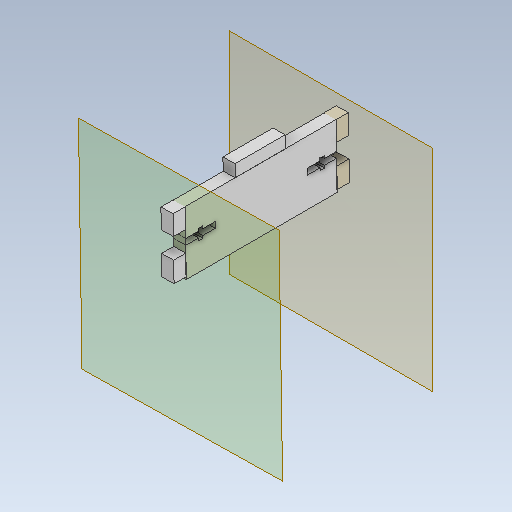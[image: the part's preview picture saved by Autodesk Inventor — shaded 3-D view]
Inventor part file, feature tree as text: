
AUTODESK INVENTOR PART (.ipt)
format: ipt  version: 2021.1 (Build 251245010, 245A)  size: 203,776 bytes
history: native  units: mm
features: reference x18, other x8, extrude x5, sketch x5, projected_geometry x1
ambient origin geometry x8: Origin, YZ Plane, XZ Plane, XY Plane, X Axis, Y Axis, Z Axis, Center Point
bodies: Body1 (feature_tree)
feature tree (37):
  other  "Твердое тело1"
  other  "РабПлоскость1"
  extrude  "Выдавливание1"  Depth=6.2mm
  other  "РабПлоскость2"
  extrude  "Выдавливание2"  TaperAngle=0.0deg  [1 undecoded]
  extrude  "Выдавливание3"  Depth=6.2mm
  extrude  "Выдавливание4"  TaperAngle=0.0deg  [1 undecoded]
  extrude  "Выдавливание5"  Depth=6.2mm
  sketch  "Эскиз1"
  sketch  "Эскиз2"
  sketch  "Эскиз3"
  reference  "Ссылка11"
  reference  "Ссылка12"
  projected_geometry  "Спроецированная петля1"
  sketch  "Эскиз4"
  reference  "Ссылка30"
  reference  "Ссылка31"
  sketch  "Эскиз5"
  reference  "Ссылка32"
  reference  "Ссылка33"
  reference  "Ссылка34"
  reference  "Ссылка35"
  reference  "Ссылка36"
  reference  "Ссылка37"
  reference  "Ссылка38"
  reference  "Ссылка39"
  reference  "Ссылка40"
  reference  "Ссылка41"
  reference  "Ссылка42"
  reference  "Ссылка43"
  reference  "Ссылка44"
  reference  "Ссылка45"
  other  "<userpath>\Documents\Savka\3d\Korp.iam"
  other  "Korp.iam"
  other  "Деталь1:1"
  other  "Korpus 5:1"
  other  "Korpus 3:1"
note: 2 required parameter values undecoded (feature->parameter linkage not recoverable at this tier; creation-order binding heuristic only, values carry confidence <= 0.55)
